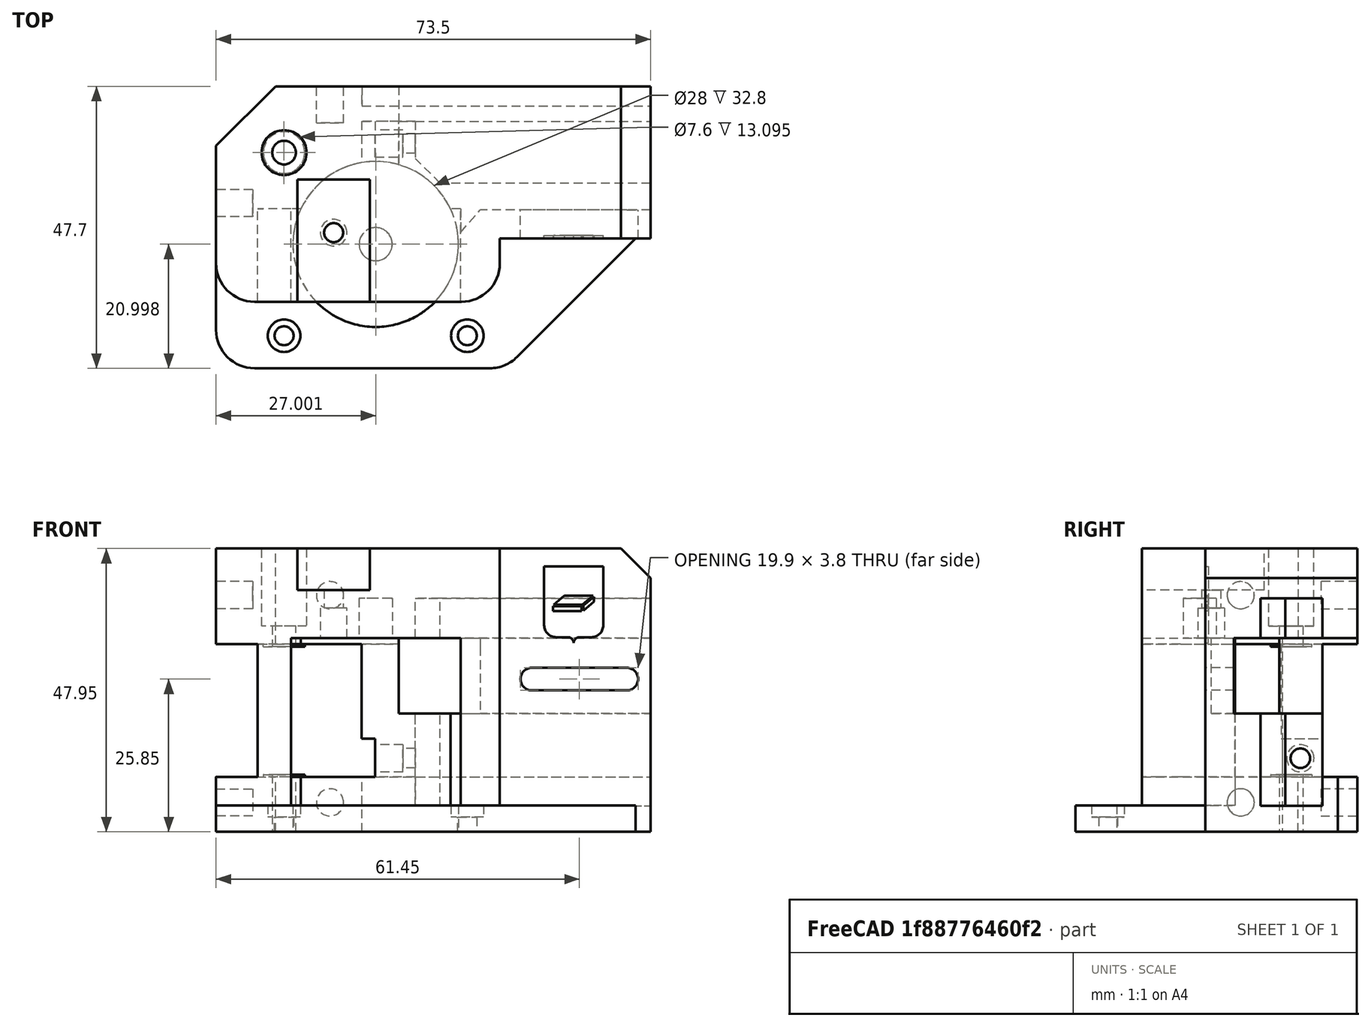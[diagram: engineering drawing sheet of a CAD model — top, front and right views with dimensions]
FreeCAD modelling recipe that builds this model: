
FCSTD DOCUMENT  (FreeCAD 1.0R38641 +468 (Git))
Label: k1_motor_mount_left
License: All rights reserved
LicenseURL: https://en.wikipedia.org/wiki/All_rights_reserved
objects: App::Link×4, Part::Feature×1, PartDesign::FeatureBase×1, PartDesign::Body×1, App::Part×1
note: 4 computed .brp shape members not serialized (recipe doc carries the construction recipe); baked Part::Feature solids carry a one-line shape summary decoded from their .brp
EXTERNAL_REF file=cad_powge_pulley.FCStd obj=Part
EXTERNAL_REF file=cad_nema17_42_60.FCStd obj=COMPOUND049
EXTERNAL_REF file=cad_20T_15mm_pulley.FCStd obj=Part

FEATURE [Part::Feature] Part__Feature  label="step"
  shape: bbox 73.5 x 47.7 x 47.95 mm, 115 faces (baked)
FEATURE [PartDesign::FeatureBase] BaseFeature
  BaseFeature = -> Part__Feature
  Suppressed = false
FEATURE [PartDesign::Body] Body  label="k1_motor_mount_left"
  AllowCompound = false
  BaseFeature = -> Part__Feature
  Group = -> [BaseFeature]
  Origin = -> Origin
  Placement = pos=(-52,-950,0) rot=(0,0,1;0rad)
  Tip = -> BaseFeature
FEATURE [App::Link] Link  label="cad_powge_pulley_top_link"
  LinkPlacement = pos=(12.1406,50.0783,20.85) rot=(0,0,1;0rad)
  LinkedObject = -> <external cad_powge_pulley.FCStd>#Part
  Placement = pos=(12.1406,50.0783,20.85) rot=(0,0,1;0rad)
FEATURE [App::Link] Link001  label="cad_powge_pulley_bottom_link"
  LinkPlacement = pos=(12.1406,50.0783,9.7) rot=(0,0,1;0rad)
  LinkedObject = -> <external cad_powge_pulley.FCStd>#Part
  Placement = pos=(12.1406,50.0783,9.7) rot=(0,0,1;0rad)
FEATURE [App::Link] Link002  label="cad_nema17_link"
  LinkPlacement = pos=(27.6406,34.5783,-16.802) rot=(0,0,1;0rad)
  LinkedObject = -> <external cad_nema17_42_60.FCStd>#COMPOUND049
  Placement = pos=(27.6406,34.5783,-16.802) rot=(0,0,1;0rad)
FEATURE [App::Link] Link003  label="cad_20T_pulley"
  LinkPlacement = pos=(115.263,-34.4991,1.64211) rot=(0,1,0;3.14159rad)
  LinkedObject = -> <external cad_20T_15mm_pulley.FCStd>#Part
  Placement = pos=(115.263,-34.4991,1.64211) rot=(0,1,0;3.14159rad)
FEATURE [App::Part] Part  label="k1_motor_mount_left_part"
  Group = -> [Part__Feature,Body,Link,Link001,Link002,Link003]
  Origin = -> Origin001

RESOLVED EXTERNAL PARTS (link-assembly join: the EXTERNAL_REF files above that resolve inside this repo's crawl, each included once):
---- part cad_powge_pulley.FCStd = doc fcstd_d49da9a9e340 ----
FCSTD DOCUMENT  (FreeCAD 1.0R38641 +468 (Git))
Label: cad_powge_pulley
License: All rights reserved
LicenseURL: https://en.wikipedia.org/wiki/All_rights_reserved
objects: Sketcher::SketchObject×1, PartDesign::Revolution×1, PartDesign::Body×1, App::Part×1
note: 6 computed .brp shape members not serialized (recipe doc carries the construction recipe); baked Part::Feature solids carry a one-line shape summary decoded from their .brp

FEATURE [Sketcher::SketchObject] Sketch
  ArcFitTolerance = 1e-06
  AttachmentSupport = -> [XZ_Plane]
  FullyConstrained = true
  MakeInternals = false
  MapMode = 5
  Placement = pos=(0,0,0) rot=(1,0,0;1.5708rad)
  sketch-geometry (8):
    g0: LineSegment StartX=6.1 StartY=9.3 StartZ=0 EndX=6.1 EndY=1.2 EndZ=0
    g1: LineSegment StartX=6.1 StartY=1.2 StartZ=0 EndX=8 EndY=1.2 EndZ=0
    g2: LineSegment StartX=8 StartY=1.2 StartZ=0 EndX=8 EndY=0 EndZ=0
    g3: LineSegment StartX=8 StartY=0 StartZ=0 EndX=2 EndY=0 EndZ=0
    g4: LineSegment StartX=2 StartY=0 StartZ=0 EndX=2 EndY=10.5 EndZ=0
    g5: LineSegment StartX=2 StartY=10.5 StartZ=0 EndX=8 EndY=10.5 EndZ=0
    g6: LineSegment StartX=8 StartY=10.5 StartZ=0 EndX=8 EndY=9.3 EndZ=0
    g7: LineSegment StartX=8 StartY=9.3 StartZ=0 EndX=6.1 EndY=9.3 EndZ=0
  constraints (24):
    c: Vertical(g0)
    c: Coincident(g1,g0)
    c: Horizontal(g1)
    c: Coincident(g2,g1)
    c: PointOnObject(g2,g-1)
    c: Vertical(g2)
    c: Coincident(g3,g2)
    c: PointOnObject(g3,g-1)
    c: Coincident(g4,g3)
    c: Vertical(g4)
    c: Coincident(g5,g4)
    c: Horizontal(g5)
    c: Coincident(g6,g5)
    c: Vertical(g6)
    c: Coincident(g7,g6)
    c: Horizontal(g7)
    c: Coincident(g0,g7)
    c: Equal(g5,g3)
    c: Equal(g6,g2)
    c: Distance(g4,g-2) = 2
    c: Distance(g5,g-2) = 8
    c: DistanceY(g0,g0) = 8.1
    c: DistanceY(g4,g4) = 10.5
    c: Distance(g0,g-2) = 6.1
FEATURE [PartDesign::Revolution] Revolution
  Angle = 360
  Angle2 = 60
  Axis = (0,2e-16,1)
  Base = (0,0,0)
  Placement = pos=(0,0,0) rot=(1,0,0;1.5708rad)
  Profile = -> Sketch
  ReferenceAxis = -> Sketch [V_Axis]
  Refine = true
  Reversed = true
  Suppressed = false
  Type = 0
FEATURE [PartDesign::Body] Body  label="powge_pulley"
  AllowCompound = false
  Group = -> [Sketch,Revolution]
  Origin = -> Origin
  Tip = -> Revolution
FEATURE [App::Part] Part  label="powge_pulley_part"
  Group = -> [Body]
  Origin = -> Origin001
